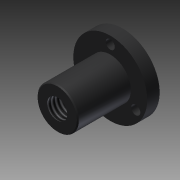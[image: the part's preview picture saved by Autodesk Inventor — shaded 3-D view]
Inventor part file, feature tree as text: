
AUTODESK INVENTOR PART (.ipt)
format: ipt  version: 2011 (Build 150239000, 239)  size: 111,104 bytes
history: native  units: mm (DEFAULTED — no unit token found)
features: sketch x4, extrude x2, hole x2, chamfer x1, pattern_circular x1
ambient origin geometry x8: Origin, YZ Plane, XZ Plane, XY Plane, X Axis, Y Axis, Z Axis, Center Point
bodies: Solid1 (feature_tree)
feature tree (10):
  extrude  "Extrusion1"  Depth=20.574mm TaperAngle=0.0deg
  extrude  "Extrusion2"  Depth=0.381mm
  hole  "Hole2"  [1 undecoded]
  chamfer  "Chamfer1"  Distance=30.0mm Angle=360.0deg
  hole  "Hole3"  [1 undecoded]
  pattern_circular  "Circular Pattern1"  [2 undecoded]
  sketch  "Sketch1"  dims[d0=16.002mm d1=20.574mm d2=0.0mm]
  sketch  "Sketch2"  dims[d4=4.826mm d5=0.0mm]
  sketch  "Sketch4"  dims[d17=7.7978mm d18=6.0mm d19=4.0mm d20=2.0mm d21=14.3117mm d22=8.0mm d23=20.594885mm d26=0.381mm d27=3.175mm]
  sketch  "Sketch6"  dims[d28=45.0deg d29=28.702mm d30=3.556mm d31=12.7mm d32=9.525mm d33=6.35mm d34=14.3117mm d35=19.05mm d36=20.594885mm d37=30.0mm d38=360.0deg]
note: 4 required parameter values undecoded (feature->parameter linkage not recoverable at this tier; creation-order binding heuristic only, values carry confidence <= 0.55)
